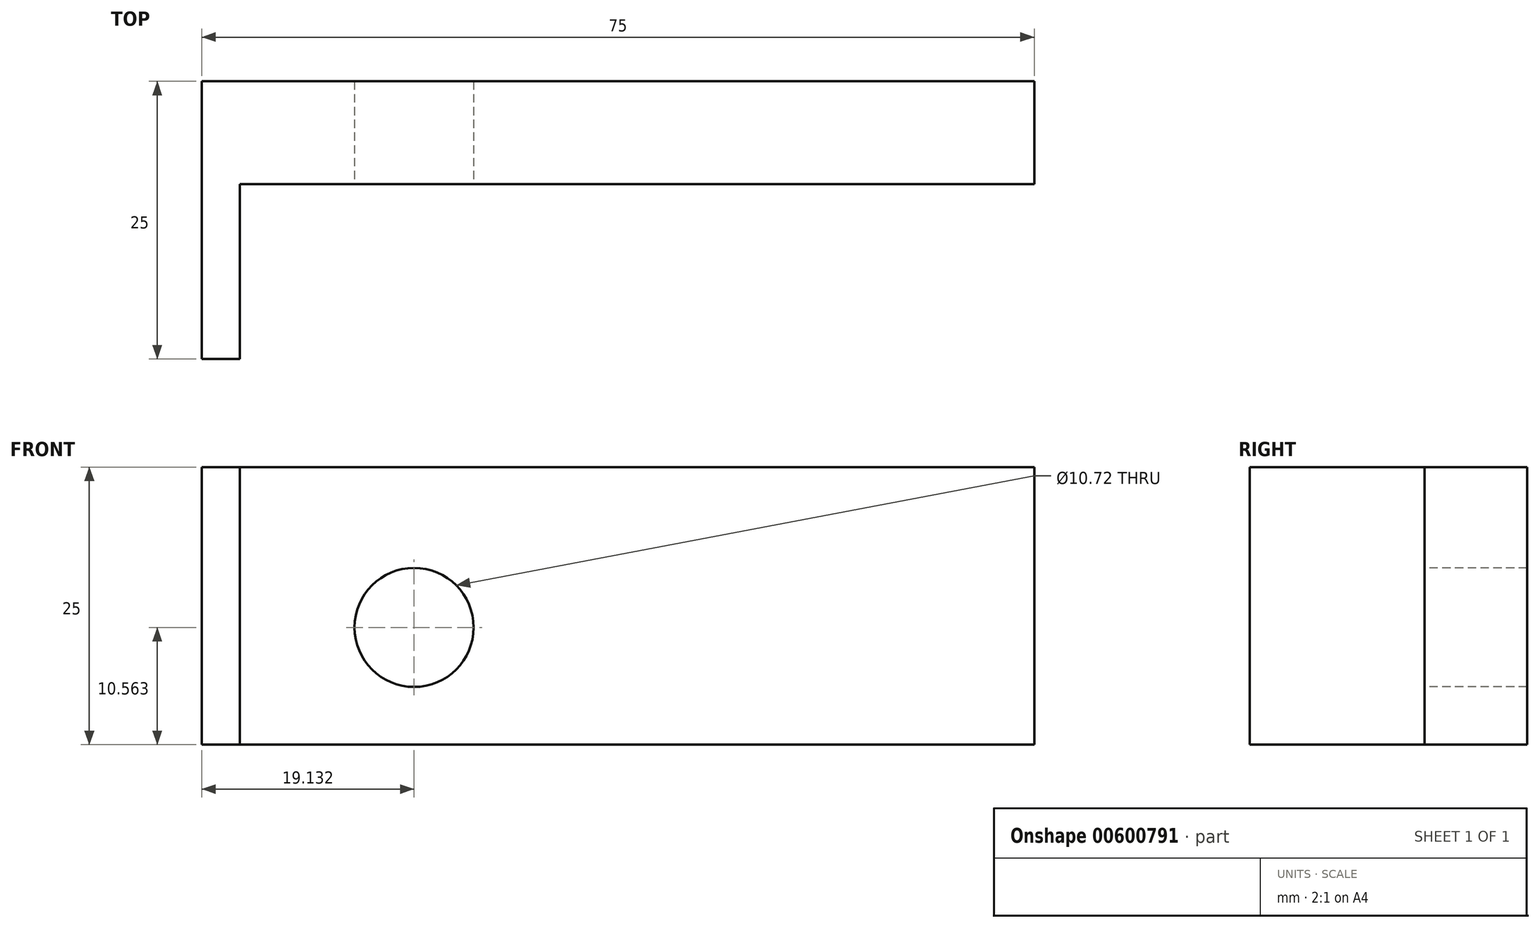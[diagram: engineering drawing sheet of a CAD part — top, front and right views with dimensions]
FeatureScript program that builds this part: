
annotation { "Feature Type Name" : "Feature", "Feature Type Description" : "" }
export const myFeature = defineFeature(function(context is Context, id is Id, definition is map)
    precondition{}
    {
        {
            var Q0;
            Q0=qCreatedBy(makeId("Top.planeOp"),FACE);
            var sketch = newSketch(context, id + "F0", { "sketchPlane" : qUnion([Q0])});
            skLineSegment(sketch, "E0.bottom", {"start": v(-36.44, 11.23) * mm, "end": v(38.56, 11.23) * mm});
            skLineSegment(sketch, "E0.top", {"start": v(-36.44, -13.77) * mm, "end": v(38.56, -13.77) * mm});
            skLineSegment(sketch, "E0.left", {"start": v(-36.44, 11.23) * mm, "end": v(-36.44, -13.77) * mm});
            skLineSegment(sketch, "E0.right", {"start": v(38.56, 11.23) * mm, "end": v(38.56, -13.77) * mm});
            skSolve(sketch);
        }
        {
            var Q0;
            Q0 = qSketchRegion(id + "F0", true);
            extrude(context, id + "F1", {"entities" : qUnion([Q0]), "depth" : 25 * mm, "offsetDistance" : 25 * mm});
        }
        {
            var Q0;
            Q0=makeQuery(id+"F1.opExtrude","CAP_FACE",FACE,{"disambiguationData":[OSD([sQuery(id+"F0.wireOp",EDGE,"E0.bottom"),sQuery(id+"F0.wireOp",EDGE,"E0.top"),sQuery(id+"F0.wireOp",EDGE,"E0.left"),sQuery(id+"F0.wireOp",EDGE,"E0.right")])],"isStart":false});
            var sketch = newSketch(context, id + "F2", { "sketchPlane" : qUnion([Q0])});
            skLineSegment(sketch, "E1.bottom", {"start": v(-32.99, 1.98) * mm, "end": v(38.56, 1.98) * mm});
            skLineSegment(sketch, "E1.top", {"start": v(-32.99, -13.77) * mm, "end": v(38.56, -13.77) * mm});
            skLineSegment(sketch, "E1.left", {"start": v(-32.99, 1.98) * mm, "end": v(-32.99, -13.77) * mm});
            skLineSegment(sketch, "E1.right", {"start": v(38.56, 1.98) * mm, "end": v(38.56, -13.77) * mm});
            skSolve(sketch);
        }
        {
            var Q0;
            Q0=makeQuery(id+"F2.imprint","IMPRINT",FACE,{"disambiguationData":[TD([[makeQuery(id+"F2.imprint","IMPRINT",EDGE,{"derivedFrom":sQuery(id+"F2.wireOp",EDGE,"E1.bottom")}),-1.0]])]});
            extrude(context, id + "F3", {"entities" : qUnion([Q0]), "operationType" : NewBodyOperationType.REMOVE, "oppositeDirection" : true, "depth" : 25 * mm, "offsetDistance" : 25 * mm});
        }
        {
            var Q0;
            Q0=makeQuery(id+"F3.boolean.opBoolean","COPY",FACE,{"derivedFrom":makeQuery(id+"F3.opExtrude","SWEPT_FACE",FACE,{"disambiguationData":[OSD([sQuery(id+"F2.wireOp",EDGE,"E1.bottom")])]})});
            var sketch = newSketch(context, id + "F4", { "sketchPlane" : qUnion([Q0])});
            skCircle(sketch, "E2", {"center": v(-17.3, 10.56) * mm, "radius": 5.36 * mm});
            skSolve(sketch);
        }
        {
            var Q0;
            Q0=makeQuery(id+"F4.imprint","IMPRINT",FACE,{"disambiguationData":[TD([[makeQuery(id+"F4.imprint","IMPRINT",EDGE,{"derivedFrom":sQuery(id+"F4.wireOp",EDGE,"E2")}),1.0]])]});
            extrude(context, id + "F5", {"entities" : qUnion([Q0]), "operationType" : NewBodyOperationType.REMOVE, "oppositeDirection" : true, "depth" : 25 * mm, "offsetDistance" : 25 * mm});
        }
    });
